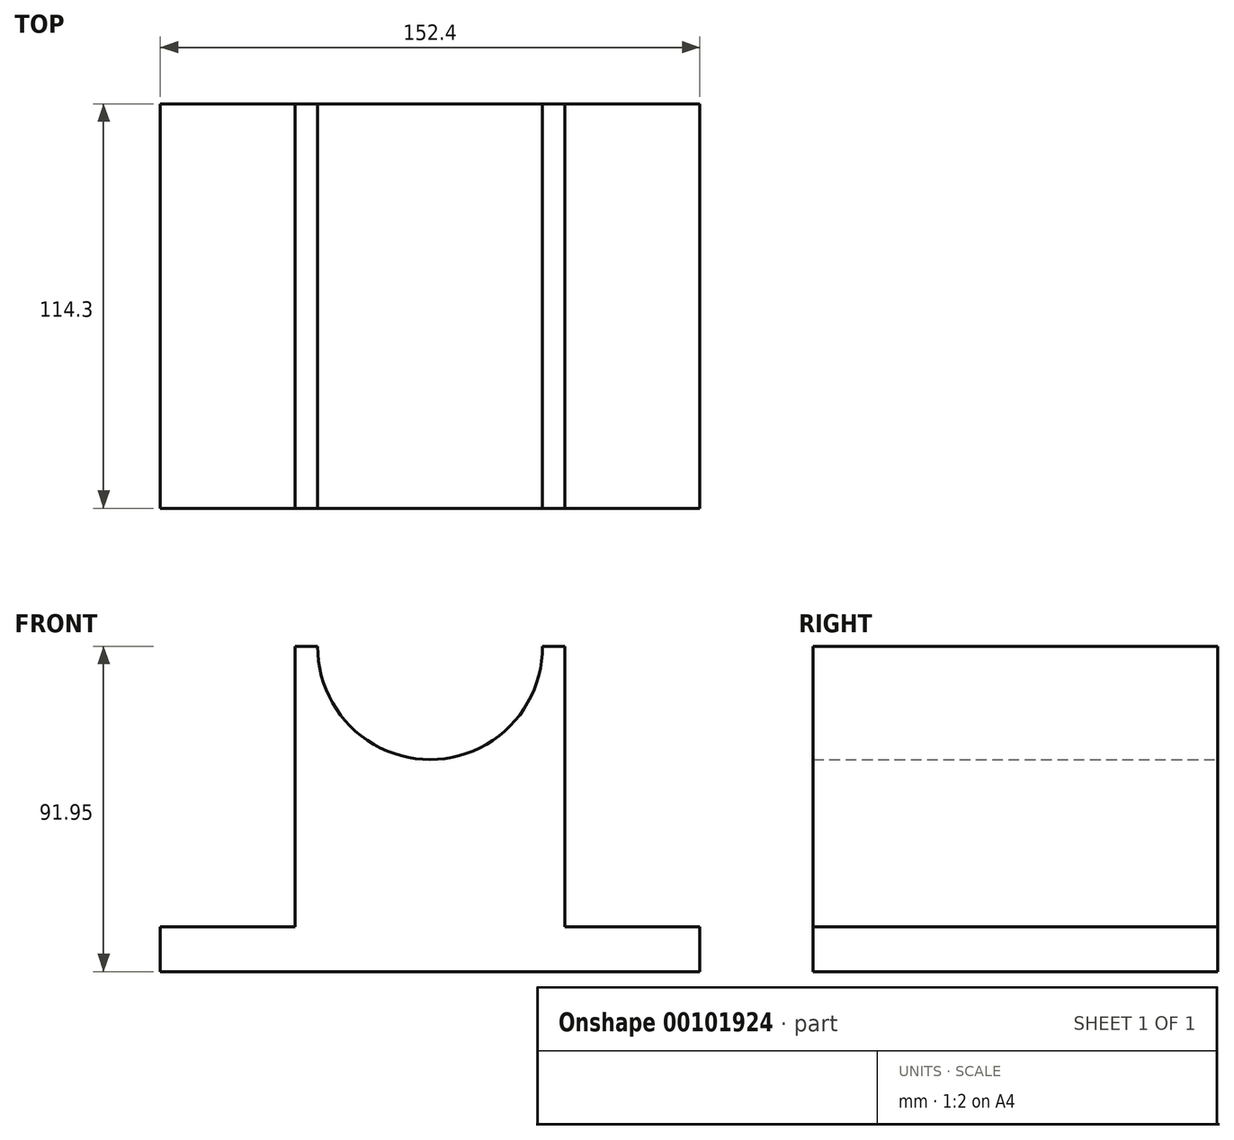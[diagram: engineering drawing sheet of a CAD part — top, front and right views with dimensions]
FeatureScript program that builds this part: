
annotation { "Feature Type Name" : "Feature", "Feature Type Description" : "" }
export const myFeature = defineFeature(function(context is Context, id is Id, definition is map)
    precondition{}
    {
        {
            var Q0;
            Q0=qCreatedBy(makeId("Front.planeOp"),FACE);
            var sketch = newSketch(context, id + "F0", { "sketchPlane" : qUnion([Q0])});
            skLineSegment(sketch, "E0.bottom", {"start": v(-82.65, -25.6) * mm, "end": v(69.75, -25.6) * mm});
            skLineSegment(sketch, "E0.top", {"start": v(-82.65, -38.3) * mm, "end": v(69.75, -38.3) * mm});
            skLineSegment(sketch, "E0.left", {"start": v(-82.65, -25.6) * mm, "end": v(-82.65, -38.3) * mm});
            skLineSegment(sketch, "E0.right", {"start": v(69.75, -25.6) * mm, "end": v(69.75, -38.3) * mm});
            skLineSegment(sketch, "E1.bottom", {"start": v(-44.55, -25.6) * mm, "end": v(31.65, -25.6) * mm});
            skLineSegment(sketch, "E1.top", {"start": v(-44.55, 53.66) * mm, "end": v(-38.2, 53.66) * mm});
            skLineSegment(sketch, "E1.left", {"start": v(-44.55, -25.6) * mm, "end": v(-44.55, 53.66) * mm});
            skLineSegment(sketch, "E1.right", {"start": v(31.65, -25.6) * mm, "end": v(31.65, 53.66) * mm});
            skArc(sketch, "E2", {"start": v(-38.2, 53.66) * mm, "mid": v(-6.44, 21.65) * mm, "end": v(25.3, 53.66) * mm});
            skLineSegment(sketch, "E3.trimOffspring", {"start": v(25.3, 53.66) * mm, "end": v(31.65, 53.66) * mm});
            skSolve(sketch);
        }
        {
            var Q0;
            Q0 = qSketchRegion(id + "F0", true);
            extrude(context, id + "F1", {"entities" : qUnion([Q0]), "depth" : 114.3 * mm});
        }
    });
